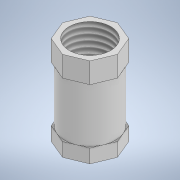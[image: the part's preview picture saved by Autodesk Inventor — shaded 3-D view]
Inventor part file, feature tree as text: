
AUTODESK INVENTOR PART (.ipt)
format: ipt  version: 2022 (Build 260153000, 153)  size: 155,648 bytes
history: native  units: mm
features: sketch x4, extrude x3, other x1, hole x1
ambient origin geometry x8: Origin, YZ Plane, XZ Plane, XY Plane, X Axis, Y Axis, Z Axis, Center Point
bodies: Body1 (feature_tree)
feature tree (9):
  other  "Sólido1"
  extrude  "Extrusión1"  Depth=5.0mm TaperAngle=0.0deg
  extrude  "Extrusión2"  Depth=20.0mm
  extrude  "Extrusión3"  [1 undecoded]
  hole  "Agujero1"  [1 undecoded]
  sketch  "Boceto1"  dims[d0=20.0mm d1=5.0mm d2=0.0mm]
  sketch  "Boceto2"  dims[d3=20.0mm d4=0.0mm d5=20.0mm]
  sketch  "Boceto3"  dims[d6=7.5mm d7=0.0mm]
  sketch  "Boceto4"  dims[d8=15.1638mm d9=32.5mm d10=4.0mm d11=2.0mm d12=90.0deg d13=8.0mm d14=20.594885mm]
note: 2 required parameter values undecoded (feature->parameter linkage not recoverable at this tier; creation-order binding heuristic only, values carry confidence <= 0.55)
